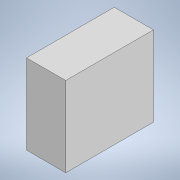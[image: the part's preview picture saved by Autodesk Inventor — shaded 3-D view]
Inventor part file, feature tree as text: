
AUTODESK INVENTOR PART (.ipt)
format: ipt  version: 2020 (Build 240168000, 168)  size: 90,112 bytes
history: native  units: mm
features: extrude x1, sketch x1
ambient origin geometry x8: Origin, YZ Plane, XZ Plane, XY Plane, X Axis, Y Axis, Z Axis, Center Point
bodies: Volumenkörper1 (feature_tree)
feature tree (2):
  extrude  "Extrusion1"  Depth=340.0mm
  sketch  "Skizze1"  dims[d0=152.0mm d1=340.0mm d2=310.0mm d3=0.0mm]
